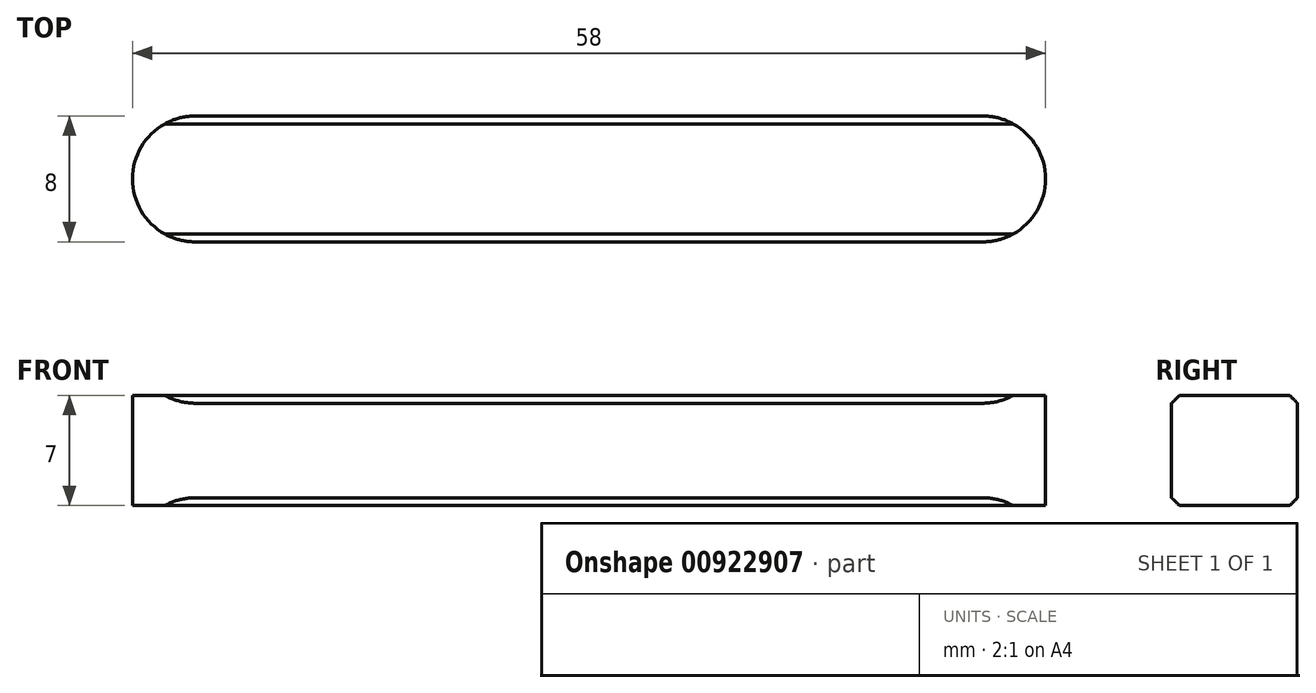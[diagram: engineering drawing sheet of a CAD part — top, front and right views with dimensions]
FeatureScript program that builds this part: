
annotation { "Feature Type Name" : "Feature", "Feature Type Description" : "" }
export const myFeature = defineFeature(function(context is Context, id is Id, definition is map)
    precondition{}
    {
        {
            var Q0;
            Q0=qCreatedBy(makeId("Top.planeOp"),FACE);
            var sketch = newSketch(context, id + "F0", { "sketchPlane" : qUnion([Q0])});
            skLineSegment(sketch, "E0.bottom", {"start": v(25, -4) * mm, "end": v(-25, -4) * mm});
            skLineSegment(sketch, "E0.top", {"start": v(25, 4) * mm, "end": v(-25, 4) * mm});
            skLineSegment(sketch, "E0.left", {"start": v(25, -4) * mm, "end": v(25, 4) * mm, "construction": true});
            skLineSegment(sketch, "E0.right", {"start": v(-25, -4) * mm, "end": v(-25, 4) * mm, "construction": true});
            skPoint(sketch, "E0.middle", {"position": v(0, 0) * mm});
            skArc(sketch, "E1", {"start": v(25, -4) * mm, "mid": v(29, 0) * mm, "end": v(25, 4) * mm});
            skArc(sketch, "E2", {"start": v(-25, 4) * mm, "mid": v(-29, 0) * mm, "end": v(-25, -4) * mm});
            skSolve(sketch);
        }
        {
            var Q0;
            Q0=makeQuery(id+"F0.imprint","IMPRINT",FACE,{"disambiguationData":[TD([[makeQuery(id+"F0.imprint","IMPRINT",EDGE,{"derivedFrom":sQuery(id+"F0.wireOp",EDGE,"E0.bottom")}),-1.0]])]});
            extrude(context, id + "F1", {"entities" : qUnion([Q0]), "depth" : 7 * mm, "offsetDistance" : 25 * mm});
        }
        {
            var Q0;
            Q0=makeQuery(id+"F1.opExtrude","CAP_EDGE",EDGE,{"disambiguationData":[OSD([sQuery(id+"F0.wireOp",EDGE,"E0.bottom")])],"isStart":false});
            var Q1;
            Q1=makeQuery(id+"F1.opExtrude","CAP_EDGE",EDGE,{"disambiguationData":[OSD([sQuery(id+"F0.wireOp",EDGE,"E0.top")])],"isStart":false});
            var Q2;
            Q2=makeQuery(id+"F1.opExtrude","CAP_EDGE",EDGE,{"disambiguationData":[OSD([sQuery(id+"F0.wireOp",EDGE,"E0.bottom")])],"isStart":true});
            var Q3;
            Q3=makeQuery(id+"F1.opExtrude","CAP_EDGE",EDGE,{"disambiguationData":[OSD([sQuery(id+"F0.wireOp",EDGE,"E0.top")])],"isStart":true});
            chamfer(context, id + "F2", {"entities" : qUnion([Q0, Q1, Q2, Q3]), "width" : 0.5 * mm});
        }
    });
